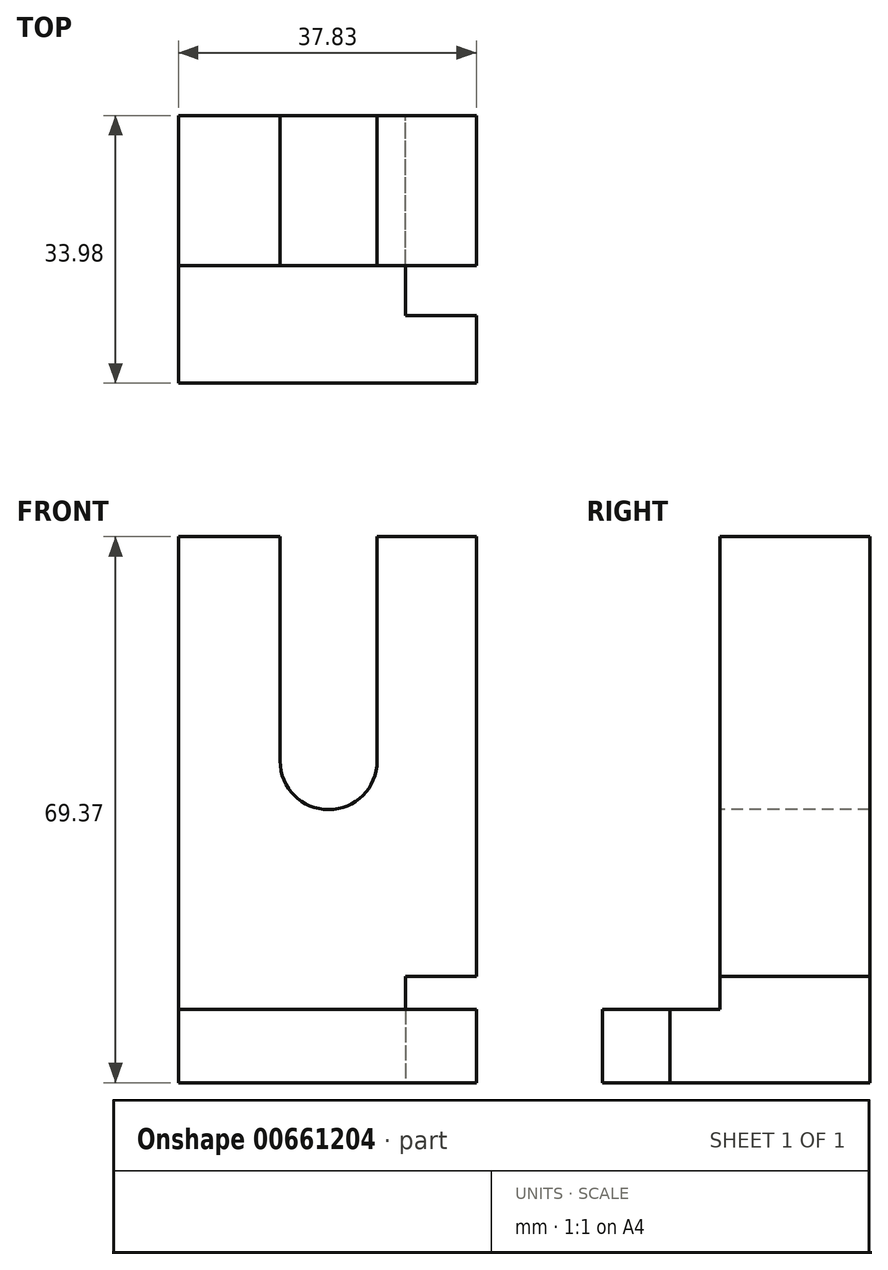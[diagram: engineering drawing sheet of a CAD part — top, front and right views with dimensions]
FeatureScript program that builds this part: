
annotation { "Feature Type Name" : "Feature", "Feature Type Description" : "" }
export const myFeature = defineFeature(function(context is Context, id is Id, definition is map)
    precondition{}
    {
        {
            var Q0;
            Q0=qCreatedBy(makeId("Front.planeOp"),FACE);
            var sketch = newSketch(context, id + "F0", { "sketchPlane" : qUnion([Q0])});
            skLineSegment(sketch, "E0.bottom", {"start": v(0, 0) * mm, "end": v(-37.83, 0) * mm});
            skLineSegment(sketch, "E0.top", {"start": v(0, 55.84) * mm, "end": v(-37.83, 55.84) * mm});
            skLineSegment(sketch, "E0.left", {"start": v(0, 0) * mm, "end": v(0, 55.84) * mm});
            skLineSegment(sketch, "E0.right", {"start": v(-37.83, 0) * mm, "end": v(-37.83, 55.84) * mm});
            skSolve(sketch);
        }
        {
            var Q0;
            Q0=makeQuery(id+"F0.imprint","IMPRINT",FACE,{"disambiguationData":[TD([[makeQuery(id+"F0.imprint","IMPRINT",EDGE,{"derivedFrom":sQuery(id+"F0.wireOp",EDGE,"E0.bottom")}),-1.0]])]});
            extrude(context, id + "F1", {"entities" : qUnion([Q0]), "depth" : 19.05 * mm, "offsetDistance" : 25.4 * mm});
        }
        {
            var Q0;
            Q0=makeQuery(id+"F1.opExtrude","CAP_FACE",FACE,{"disambiguationData":[OSD([sQuery(id+"F0.wireOp",EDGE,"E0.bottom"),sQuery(id+"F0.wireOp",EDGE,"E0.top"),sQuery(id+"F0.wireOp",EDGE,"E0.left"),sQuery(id+"F0.wireOp",EDGE,"E0.right")])],"isStart":false});
            var sketch = newSketch(context, id + "F2", { "sketchPlane" : qUnion([Q0])});
            skLineSegment(sketch, "E1", {"start": v(-24.92, 55.84) * mm, "end": v(-24.92, 27.32) * mm});
            skLineSegment(sketch, "E2", {"start": v(-12.6, 55.84) * mm, "end": v(-12.6, 27.32) * mm});
            skArc(sketch, "E3", {"start": v(-24.92, 27.32) * mm, "mid": v(-18.76, 21.16) * mm, "end": v(-12.6, 27.32) * mm});
            skLineSegment(sketch, "E4", {"start": v(-24.92, 55.84) * mm, "end": v(-12.6, 55.84) * mm});
            skSolve(sketch);
        }
        {
            var Q0;
            Q0=makeQuery(id+"F2.imprint","IMPRINT",FACE,{"disambiguationData":[TD([[makeQuery(id+"F2.imprint","IMPRINT",EDGE,{"derivedFrom":sQuery(id+"F2.wireOp",EDGE,"E1")}),1.0]])]});
            extrude(context, id + "F3", {"entities" : qUnion([Q0]), "operationType" : NewBodyOperationType.REMOVE, "oppositeDirection" : true, "depth" : 19.05 * mm, "offsetDistance" : 25.4 * mm});
        }
        {
            var Q0;
            Q0=qCreatedBy(makeId("Front.planeOp"),FACE);
            var sketch = newSketch(context, id + "F4", { "sketchPlane" : qUnion([Q0])});
            skLineSegment(sketch, "E5.bottom", {"start": v(-37.83, 0) * mm, "end": v(-9.02, 0) * mm});
            skLineSegment(sketch, "E5.top", {"start": v(-37.83, -13.53) * mm, "end": v(-9.02, -13.53) * mm});
            skLineSegment(sketch, "E5.left", {"start": v(-37.83, 0) * mm, "end": v(-37.83, -13.53) * mm});
            skLineSegment(sketch, "E5.right", {"start": v(-9.02, 0) * mm, "end": v(-9.02, -13.53) * mm});
            skSolve(sketch);
        }
        {
            var Q0;
            Q0=makeQuery(id+"F4.imprint","IMPRINT",FACE,{"disambiguationData":[TD([[makeQuery(id+"F4.imprint","IMPRINT",EDGE,{"derivedFrom":sQuery(id+"F4.wireOp",EDGE,"E5.bottom")}),-1.0]])]});
            extrude(context, id + "F5", {"entities" : qUnion([Q0]), "operationType" : NewBodyOperationType.ADD, "depth" : 25.4 * mm, "offsetDistance" : 25.4 * mm});
        }
        {
            var Q0;
            Q0=makeQuery(id+"F5.opExtrude","SWEPT_FACE",FACE,{"disambiguationData":[OSD([sQuery(id+"F4.wireOp",EDGE,"E5.right")])]});
            var sketch = newSketch(context, id + "F6", { "sketchPlane" : qUnion([Q0])});
            skLineSegment(sketch, "E6", {"start": v(-19.05, 0) * mm, "end": v(-19.05, -4.2) * mm});
            skLineSegment(sketch, "E7", {"start": v(-19.05, -4.2) * mm, "end": v(-25.4, -4.2) * mm});
            skLineSegment(sketch, "E8", {"start": v(-25.4, -4.2) * mm, "end": v(-25.4, 0) * mm});
            skLineSegment(sketch, "E9", {"start": v(-25.4, 0) * mm, "end": v(-19.05, 0) * mm});
            skSolve(sketch);
        }
        {
            var Q0;
            Q0=makeQuery(id+"F6.imprint","IMPRINT",FACE,{"disambiguationData":[TD([[makeQuery(id+"F6.imprint","IMPRINT",EDGE,{"derivedFrom":sQuery(id+"F6.wireOp",EDGE,"E6")}),-1.0]])]});
            extrude(context, id + "F7", {"entities" : qUnion([Q0]), "operationType" : NewBodyOperationType.REMOVE, "oppositeDirection" : true, "depth" : 76.2 * mm, "offsetDistance" : 25.4 * mm});
        }
        {
            var Q0;
            Q0=makeQuery(id+"F5.opExtrude","SWEPT_FACE",FACE,{"disambiguationData":[OSD([sQuery(id+"F4.wireOp",EDGE,"E5.right")])]});
            var sketch = newSketch(context, id + "F8", { "sketchPlane" : qUnion([Q0])});
            skLineSegment(sketch, "E10", {"start": v(-25.4, -4.2) * mm, "end": v(-33.98, -4.2) * mm});
            skLineSegment(sketch, "E11", {"start": v(-33.98, -4.2) * mm, "end": v(-33.98, -13.53) * mm});
            skLineSegment(sketch, "E12", {"start": v(-33.98, -13.53) * mm, "end": v(-25.4, -13.53) * mm});
            skSolve(sketch);
        }
        {
            var Q0;
            Q0=makeQuery(id+"F8.imprint","IMPRINT",FACE,{"disambiguationData":[TD([[makeQuery(id+"F8.imprint","IMPRINT",EDGE,{"derivedFrom":sQuery(id+"F8.wireOp",EDGE,"E10")}),1.0]])]});
            extrude(context, id + "F9", {"entities" : qUnion([Q0]), "operationType" : NewBodyOperationType.ADD, "oppositeDirection" : true, "depth" : 28.8 * mm, "offsetDistance" : 25.4 * mm});
        }
        {
            var Q0;
            Q0=makeQuery(id+"F8.imprint","IMPRINT",FACE,{"disambiguationData":[TD([[makeQuery(id+"F8.imprint","IMPRINT",EDGE,{"derivedFrom":sQuery(id+"F8.wireOp",EDGE,"E10")}),1.0]])]});
            extrude(context, id + "F10", {"entities" : qUnion([Q0]), "operationType" : NewBodyOperationType.ADD, "depth" : 9.02 * mm, "offsetDistance" : 25.4 * mm});
        }
    });
